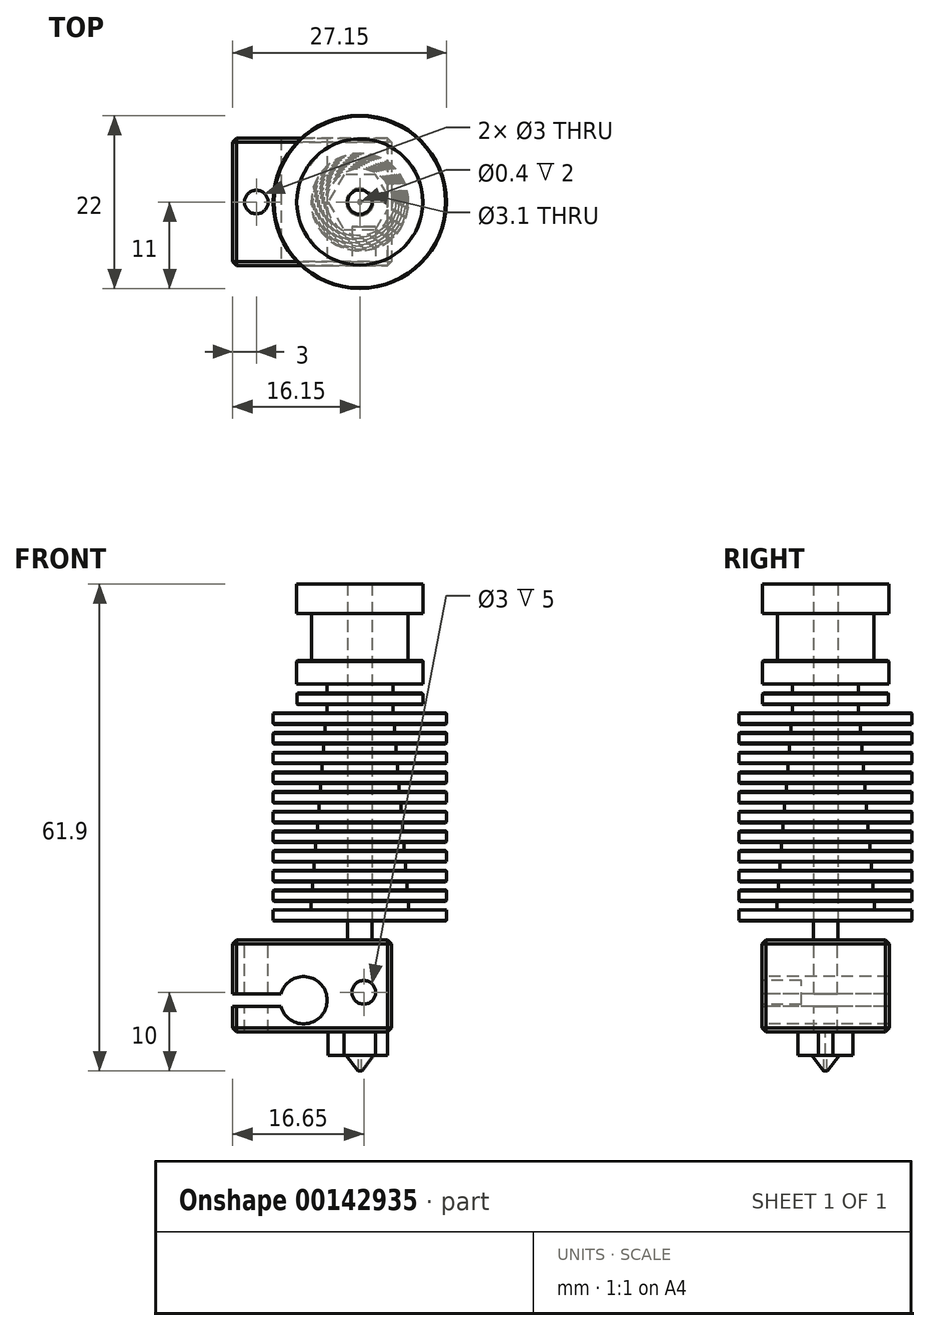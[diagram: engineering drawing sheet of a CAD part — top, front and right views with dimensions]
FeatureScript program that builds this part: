
annotation { "Feature Type Name" : "Feature", "Feature Type Description" : "" }
export const myFeature = defineFeature(function(context is Context, id is Id, definition is map)
    precondition{}
    {
        {
            var Q0;
            Q0=qCreatedBy(makeId("Top.planeOp"),FACE);
            var sketch = newSketch(context, id + "F0", { "sketchPlane" : qUnion([Q0])});
            skCircle(sketch, "E0", {"center": v(0, 0) * mm, "radius": 11 * mm});
            skCircle(sketch, "E1", {"center": v(0, 0) * mm, "radius": 1.55 * mm});
            skSolve(sketch);
        }
        {
            var Q0;
            Q0 = qSketchRegion(id + "F0", true);
            extrude(context, id + "F1", {"entities" : qUnion([Q0]), "depth" : 42.85 * mm});
        }
        {
            var Q0;
            Q0=qCreatedBy(makeId("Front.planeOp"),FACE);
            var sketch = newSketch(context, id + "F2", { "sketchPlane" : qUnion([Q0])});
            skLineSegment(sketch, "E2", {"start": v(11, 0) * mm, "end": v(11, 1.45) * mm});
            skLineSegment(sketch, "E3", {"start": v(11, 1.45) * mm, "end": v(6.2, 1.45) * mm});
            skLineSegment(sketch, "E4", {"start": v(6.2, 1.45) * mm, "end": v(6.2, 2.5) * mm});
            skLineSegment(sketch, "E5", {"start": v(6.2, 2.5) * mm, "end": v(11, 2.5) * mm});
            skLineSegment(sketch, "E6", {"start": v(11, 2.5) * mm, "end": v(11, 3.95) * mm});
            skLineSegment(sketch, "E7", {"start": v(11, 3.95) * mm, "end": v(6, 3.95) * mm});
            skLineSegment(sketch, "E8", {"start": v(6, 3.95) * mm, "end": v(6, 5) * mm});
            skLineSegment(sketch, "E9", {"start": v(6, 5) * mm, "end": v(11, 5) * mm});
            skLineSegment(sketch, "E10", {"start": v(11, 5) * mm, "end": v(11, 6.45) * mm});
            skLineSegment(sketch, "E11", {"start": v(11, 6.45) * mm, "end": v(5.8, 6.45) * mm});
            skLineSegment(sketch, "E12", {"start": v(5.8, 6.45) * mm, "end": v(5.8, 7.5) * mm});
            skLineSegment(sketch, "E13", {"start": v(5.8, 7.5) * mm, "end": v(11, 7.5) * mm});
            skLineSegment(sketch, "E14", {"start": v(11, 7.5) * mm, "end": v(11, 8.95) * mm});
            skLineSegment(sketch, "E15", {"start": v(11, 8.95) * mm, "end": v(5.6, 8.95) * mm});
            skLineSegment(sketch, "E16", {"start": v(5.6, 8.95) * mm, "end": v(5.6, 10) * mm});
            skLineSegment(sketch, "E17", {"start": v(5.6, 10) * mm, "end": v(11, 10) * mm});
            skLineSegment(sketch, "E18", {"start": v(11, 10) * mm, "end": v(11, 11.45) * mm});
            skLineSegment(sketch, "E19", {"start": v(11, 11.45) * mm, "end": v(5.4, 11.45) * mm});
            skLineSegment(sketch, "E20", {"start": v(5.4, 11.45) * mm, "end": v(5.4, 12.5) * mm});
            skLineSegment(sketch, "E21", {"start": v(5.4, 12.5) * mm, "end": v(11, 12.5) * mm});
            skLineSegment(sketch, "E22", {"start": v(11, 12.5) * mm, "end": v(11, 13.95) * mm});
            skLineSegment(sketch, "E23", {"start": v(11, 13.95) * mm, "end": v(5.2, 13.95) * mm});
            skLineSegment(sketch, "E24", {"start": v(5.2, 13.95) * mm, "end": v(5.2, 15) * mm});
            skLineSegment(sketch, "E25", {"start": v(5.2, 15) * mm, "end": v(11, 15) * mm});
            skLineSegment(sketch, "E26", {"start": v(11, 15) * mm, "end": v(11, 16.45) * mm});
            skLineSegment(sketch, "E27", {"start": v(11, 16.45) * mm, "end": v(5, 16.45) * mm});
            skLineSegment(sketch, "E28", {"start": v(5, 16.45) * mm, "end": v(5, 17.5) * mm});
            skLineSegment(sketch, "E29", {"start": v(5, 17.5) * mm, "end": v(11, 17.5) * mm});
            skLineSegment(sketch, "E30", {"start": v(11, 17.5) * mm, "end": v(11, 18.95) * mm});
            skLineSegment(sketch, "E31", {"start": v(11, 18.95) * mm, "end": v(4.8, 18.95) * mm});
            skLineSegment(sketch, "E32", {"start": v(4.8, 18.95) * mm, "end": v(4.8, 20) * mm});
            skLineSegment(sketch, "E33", {"start": v(4.8, 20) * mm, "end": v(11, 20) * mm});
            skLineSegment(sketch, "E34", {"start": v(11, 20) * mm, "end": v(11, 21.45) * mm});
            skLineSegment(sketch, "E35", {"start": v(11, 21.45) * mm, "end": v(4.6, 21.45) * mm});
            skLineSegment(sketch, "E36", {"start": v(4.6, 21.45) * mm, "end": v(4.6, 22.5) * mm});
            skLineSegment(sketch, "E37", {"start": v(4.6, 22.5) * mm, "end": v(11, 22.5) * mm});
            skLineSegment(sketch, "E38", {"start": v(11, 22.5) * mm, "end": v(11, 23.95) * mm});
            skLineSegment(sketch, "E39", {"start": v(11, 23.95) * mm, "end": v(4.4, 23.95) * mm});
            skLineSegment(sketch, "E40", {"start": v(4.4, 23.95) * mm, "end": v(4.4, 25) * mm});
            skLineSegment(sketch, "E41", {"start": v(4.4, 25) * mm, "end": v(11, 25) * mm});
            skLineSegment(sketch, "E42", {"start": v(11, 25) * mm, "end": v(11, 26.45) * mm});
            skLineSegment(sketch, "E43", {"start": v(11, 26.45) * mm, "end": v(4.2, 26.45) * mm});
            skLineSegment(sketch, "E44", {"start": v(4.2, 26.45) * mm, "end": v(4.2, 27.5) * mm});
            skLineSegment(sketch, "E45", {"start": v(4.2, 27.5) * mm, "end": v(8, 27.5) * mm});
            skLineSegment(sketch, "E46", {"start": v(8, 27.5) * mm, "end": v(8, 28.95) * mm});
            skLineSegment(sketch, "E47", {"start": v(8, 28.95) * mm, "end": v(4.2, 28.95) * mm});
            skLineSegment(sketch, "E48", {"start": v(4.2, 28.95) * mm, "end": v(4.2, 30.1) * mm});
            skLineSegment(sketch, "E49", {"start": v(4.2, 30.1) * mm, "end": v(8.02, 30.1) * mm});
            skLineSegment(sketch, "E50", {"start": v(8.02, 30.1) * mm, "end": v(8.02, 33.1) * mm});
            skLineSegment(sketch, "E51", {"start": v(8.02, 33.1) * mm, "end": v(6.13, 33.1) * mm});
            skLineSegment(sketch, "E52", {"start": v(6.13, 33.1) * mm, "end": v(6.13, 39.1) * mm});
            skLineSegment(sketch, "E53", {"start": v(6.13, 39.1) * mm, "end": v(8.02, 39.1) * mm});
            skLineSegment(sketch, "E54", {"start": v(8.02, 39.1) * mm, "end": v(8.02, 42.85) * mm});
            skLineSegment(sketch, "E55", {"start": v(8.02, 42.85) * mm, "end": v(14.4, 42.85) * mm});
            skLineSegment(sketch, "E56", {"start": v(14.4, 42.85) * mm, "end": v(14.4, 0) * mm});
            skLineSegment(sketch, "E57", {"start": v(14.4, 0) * mm, "end": v(11, 0) * mm});
            skSolve(sketch);
        }
        {
            var Q0;
            Q0 = qSketchRegion(id + "F2", true);
            var Q1;
            Q1=makeQuery(id+"F1.opExtrude","SWEPT_FACE",FACE,{"disambiguationData":[OSD([sQuery(id+"F0.wireOp",EDGE,"E0")])]});
            revolve(context, id + "F3", {"operationType" : NewBodyOperationType.REMOVE, "entities" : qUnion([Q0]), "axis" : qUnion([Q1]), "revolveType" : RevolveType.FULL, "oppositeDirection" : true});
        }
        {
            var Q0;
            Q0=makeQuery(id+"F3.boolean.opBoolean","COPY",EDGE,{"derivedFrom":makeQuery(id+"F3.opRevolve","SWEPT_EDGE",EDGE,{"disambiguationData":[OSD([sQuery(id+"F2.wireOp",EDGE,"E54"),sQuery(id+"F2.wireOp",EDGE,"E55")])]})});
            var Q1;
            Q1=makeQuery(id+"F3.boolean.opBoolean","COPY",EDGE,{"derivedFrom":makeQuery(id+"F3.opRevolve","SWEPT_EDGE",EDGE,{"disambiguationData":[OSD([sQuery(id+"F2.wireOp",EDGE,"E50"),sQuery(id+"F2.wireOp",EDGE,"E51")])]})});
            var Q2;
            Q2=makeQuery(id+"F3.boolean.opBoolean","COPY",EDGE,{"derivedFrom":makeQuery(id+"F3.opRevolve","SWEPT_EDGE",EDGE,{"disambiguationData":[OSD([sQuery(id+"F2.wireOp",EDGE,"E46"),sQuery(id+"F2.wireOp",EDGE,"E47")])]})});
            var Q3;
            Q3=makeQuery(id+"F3.boolean.opBoolean","COPY",EDGE,{"derivedFrom":makeQuery(id+"F3.opRevolve","SWEPT_EDGE",EDGE,{"disambiguationData":[OSD([sQuery(id+"F2.wireOp",EDGE,"E45"),sQuery(id+"F2.wireOp",EDGE,"E46")])]})});
            var Q4;
            Q4=makeQuery(id+"F3.boolean.opBoolean","COPY",EDGE,{"derivedFrom":makeQuery(id+"F3.opRevolve","SWEPT_EDGE",EDGE,{"disambiguationData":[OSD([sQuery(id+"F2.wireOp",EDGE,"E42"),sQuery(id+"F2.wireOp",EDGE,"E43")])]})});
            var Q5;
            Q5=makeQuery(id+"F3.boolean.opBoolean","COPY",EDGE,{"derivedFrom":makeQuery(id+"F3.opRevolve","SWEPT_EDGE",EDGE,{"disambiguationData":[OSD([sQuery(id+"F2.wireOp",EDGE,"E41"),sQuery(id+"F2.wireOp",EDGE,"E42")])]})});
            var Q6;
            Q6=makeQuery(id+"F3.boolean.opBoolean","COPY",EDGE,{"derivedFrom":makeQuery(id+"F3.opRevolve","SWEPT_EDGE",EDGE,{"disambiguationData":[OSD([sQuery(id+"F2.wireOp",EDGE,"E38"),sQuery(id+"F2.wireOp",EDGE,"E39")])]})});
            var Q7;
            Q7=makeQuery(id+"F3.boolean.opBoolean","COPY",EDGE,{"derivedFrom":makeQuery(id+"F3.opRevolve","SWEPT_EDGE",EDGE,{"disambiguationData":[OSD([sQuery(id+"F2.wireOp",EDGE,"E37"),sQuery(id+"F2.wireOp",EDGE,"E38")])]})});
            var Q8;
            Q8=makeQuery(id+"F3.boolean.opBoolean","COPY",EDGE,{"derivedFrom":makeQuery(id+"F3.opRevolve","SWEPT_EDGE",EDGE,{"disambiguationData":[OSD([sQuery(id+"F2.wireOp",EDGE,"E34"),sQuery(id+"F2.wireOp",EDGE,"E35")])]})});
            var Q9;
            Q9=makeQuery(id+"F3.boolean.opBoolean","COPY",EDGE,{"derivedFrom":makeQuery(id+"F3.opRevolve","SWEPT_EDGE",EDGE,{"disambiguationData":[OSD([sQuery(id+"F2.wireOp",EDGE,"E33"),sQuery(id+"F2.wireOp",EDGE,"E34")])]})});
            var Q10;
            Q10=makeQuery(id+"F3.boolean.opBoolean","COPY",EDGE,{"derivedFrom":makeQuery(id+"F3.opRevolve","SWEPT_EDGE",EDGE,{"disambiguationData":[OSD([sQuery(id+"F2.wireOp",EDGE,"E30"),sQuery(id+"F2.wireOp",EDGE,"E31")])]})});
            var Q11;
            Q11=makeQuery(id+"F3.boolean.opBoolean","COPY",EDGE,{"derivedFrom":makeQuery(id+"F3.opRevolve","SWEPT_EDGE",EDGE,{"disambiguationData":[OSD([sQuery(id+"F2.wireOp",EDGE,"E29"),sQuery(id+"F2.wireOp",EDGE,"E30")])]})});
            var Q12;
            Q12=makeQuery(id+"F3.boolean.opBoolean","COPY",EDGE,{"derivedFrom":makeQuery(id+"F3.opRevolve","SWEPT_EDGE",EDGE,{"disambiguationData":[OSD([sQuery(id+"F2.wireOp",EDGE,"E26"),sQuery(id+"F2.wireOp",EDGE,"E27")])]})});
            var Q13;
            Q13=makeQuery(id+"F3.boolean.opBoolean","COPY",EDGE,{"derivedFrom":makeQuery(id+"F3.opRevolve","SWEPT_EDGE",EDGE,{"disambiguationData":[OSD([sQuery(id+"F2.wireOp",EDGE,"E25"),sQuery(id+"F2.wireOp",EDGE,"E26")])]})});
            var Q14;
            Q14=makeQuery(id+"F3.boolean.opBoolean","COPY",EDGE,{"derivedFrom":makeQuery(id+"F3.opRevolve","SWEPT_EDGE",EDGE,{"disambiguationData":[OSD([sQuery(id+"F2.wireOp",EDGE,"E22"),sQuery(id+"F2.wireOp",EDGE,"E23")])]})});
            var Q15;
            Q15=makeQuery(id+"F3.boolean.opBoolean","COPY",EDGE,{"derivedFrom":makeQuery(id+"F3.opRevolve","SWEPT_EDGE",EDGE,{"disambiguationData":[OSD([sQuery(id+"F2.wireOp",EDGE,"E21"),sQuery(id+"F2.wireOp",EDGE,"E22")])]})});
            var Q16;
            Q16=makeQuery(id+"F3.boolean.opBoolean","COPY",EDGE,{"derivedFrom":makeQuery(id+"F3.opRevolve","SWEPT_EDGE",EDGE,{"disambiguationData":[OSD([sQuery(id+"F2.wireOp",EDGE,"E18"),sQuery(id+"F2.wireOp",EDGE,"E19")])]})});
            var Q17;
            Q17=makeQuery(id+"F3.boolean.opBoolean","COPY",EDGE,{"derivedFrom":makeQuery(id+"F3.opRevolve","SWEPT_EDGE",EDGE,{"disambiguationData":[OSD([sQuery(id+"F2.wireOp",EDGE,"E17"),sQuery(id+"F2.wireOp",EDGE,"E18")])]})});
            var Q18;
            Q18=makeQuery(id+"F3.boolean.opBoolean","COPY",EDGE,{"derivedFrom":makeQuery(id+"F3.opRevolve","SWEPT_EDGE",EDGE,{"disambiguationData":[OSD([sQuery(id+"F2.wireOp",EDGE,"E14"),sQuery(id+"F2.wireOp",EDGE,"E15")])]})});
            var Q19;
            Q19=makeQuery(id+"F3.boolean.opBoolean","COPY",EDGE,{"derivedFrom":makeQuery(id+"F3.opRevolve","SWEPT_EDGE",EDGE,{"disambiguationData":[OSD([sQuery(id+"F2.wireOp",EDGE,"E13"),sQuery(id+"F2.wireOp",EDGE,"E14")])]})});
            var Q20;
            Q20=makeQuery(id+"F3.boolean.opBoolean","COPY",EDGE,{"derivedFrom":makeQuery(id+"F3.opRevolve","SWEPT_EDGE",EDGE,{"disambiguationData":[OSD([sQuery(id+"F2.wireOp",EDGE,"E10"),sQuery(id+"F2.wireOp",EDGE,"E11")])]})});
            var Q21;
            Q21=makeQuery(id+"F3.boolean.opBoolean","COPY",EDGE,{"derivedFrom":makeQuery(id+"F3.opRevolve","SWEPT_EDGE",EDGE,{"disambiguationData":[OSD([sQuery(id+"F2.wireOp",EDGE,"E9"),sQuery(id+"F2.wireOp",EDGE,"E10")])]})});
            var Q22;
            Q22=makeQuery(id+"F3.boolean.opBoolean","COPY",EDGE,{"derivedFrom":makeQuery(id+"F3.opRevolve","SWEPT_EDGE",EDGE,{"disambiguationData":[OSD([sQuery(id+"F2.wireOp",EDGE,"E6"),sQuery(id+"F2.wireOp",EDGE,"E7")])]})});
            var Q23;
            Q23=makeQuery(id+"F3.boolean.opBoolean","COPY",EDGE,{"derivedFrom":makeQuery(id+"F3.opRevolve","SWEPT_EDGE",EDGE,{"disambiguationData":[OSD([sQuery(id+"F2.wireOp",EDGE,"E5"),sQuery(id+"F2.wireOp",EDGE,"E6")])]})});
            var Q24;
            Q24=makeQuery(id+"F3.boolean.opBoolean","COPY",EDGE,{"derivedFrom":makeQuery(id+"F3.opRevolve","SWEPT_EDGE",EDGE,{"disambiguationData":[OSD([sQuery(id+"F2.wireOp",EDGE,"E2"),sQuery(id+"F2.wireOp",EDGE,"E3")])]})});
            var Q25;
            Q25=makeQuery(id+"F1.opExtrude","CAP_EDGE",EDGE,{"disambiguationData":[OSD([sQuery(id+"F0.wireOp",EDGE,"E0")])],"isStart":true});
            chamfer(context, id + "F4", {"entities" : qUnion([Q0, Q1, Q2, Q3, Q4, Q5, Q6, Q7, Q8, Q9, Q10, Q11, Q12, Q13, Q14, Q15, Q16, Q17, Q18, Q19, Q20, Q21, Q22, Q23, Q24, Q25]), "width" : .1 * mm, "tangentPropagation" : true});
        }
        {
            var Q0;
            Q0=qCreatedBy(makeId("Top.planeOp"),FACE);
            cPlane(context, id + "F5", {"entities" : qUnion([Q0]), "cplaneType" : CPlaneType.OFFSET, "offset" : 2.4 * mm, "oppositeDirection" : true, "width" : 150 * mm, "height" : 150 * mm});
        }
        {
            var Q0;
            Q0=makeQuery(id+"F0.imprint","IMPRINT",FACE,{"disambiguationData":[TD([[makeQuery(id+"F0.imprint","IMPRINT",EDGE,{"derivedFrom":sQuery(id+"F0.wireOp",EDGE,"E1")}),1.0]])]});
            extrude(context, id + "F6", {"entities" : qUnion([Q0]), "operationType" : NewBodyOperationType.ADD, "oppositeDirection" : true, "depth" : 2.4 * mm});
        }
        {
            var Q0;
            Q0=qCreatedBy(id+"F5.planeOp",FACE);
            var sketch = newSketch(context, id + "F7", { "sketchPlane" : qUnion([Q0])});
            skLineSegment(sketch, "E58.bottom", {"start": v(4, -8.1) * mm, "end": v(-16.15, -8.1) * mm});
            skLineSegment(sketch, "E58.top", {"start": v(4, 8.1) * mm, "end": v(-16.15, 8.1) * mm});
            skLineSegment(sketch, "E58.left", {"start": v(4, -8.1) * mm, "end": v(4, 8.1) * mm});
            skLineSegment(sketch, "E58.right", {"start": v(-16.15, -8.1) * mm, "end": v(-16.15, 8.1) * mm});
            skLineSegment(sketch, "E59", {"start": v(-16.15, 0) * mm, "end": v(4, 0) * mm, "construction": true});
            skLineSegment(sketch, "E60", {"start": v(0, -8.1) * mm, "end": v(0, 8.1) * mm, "construction": true});
            skLineSegment(sketch, "E61", {"start": v(-13.15, -8.1) * mm, "end": v(-13.15, 8.1) * mm, "construction": true});
            skCircle(sketch, "E62", {"center": v(-13.15, 0) * mm, "radius": 1.5 * mm});
            skSolve(sketch);
        }
        {
            var Q0;
            Q0=makeQuery(id+"F7.imprint","IMPRINT",FACE,{"disambiguationData":[TD([[makeQuery(id+"F7.imprint","IMPRINT",EDGE,{"derivedFrom":sQuery(id+"F7.wireOp",EDGE,"E58.bottom")}),-1.0]])]});
            extrude(context, id + "F8", {"entities" : qUnion([Q0]), "operationType" : NewBodyOperationType.ADD, "oppositeDirection" : true, "depth" : 11.65 * mm});
        }
        {
            var Q0;
            Q0=makeQuery(id+"F8.opExtrude","SWEPT_FACE",FACE,{"disambiguationData":[OSD([sQuery(id+"F7.wireOp",EDGE,"E58.bottom")])]});
            var sketch = newSketch(context, id + "F9", { "sketchPlane" : qUnion([Q0])});
            skCircle(sketch, "E63", {"center": v(0.5, -9.05) * mm, "radius": 1.5 * mm});
            skArc(sketch, "E64", {"start": v(-10.04, -10.85) * mm, "mid": v(-4.15, -10.05) * mm, "end": v(-10.04, -9.25) * mm});
            skLineSegment(sketch, "E65", {"start": v(-10.04, -9.25) * mm, "end": v(-16.15, -9.25) * mm});
            skLineSegment(sketch, "E66", {"start": v(-10.04, -10.85) * mm, "end": v(-16.15, -10.85) * mm});
            skSolve(sketch);
        }
        {
            var Q0;
            Q0 = qSketchRegion(id + "F9", true);
            extrude(context, id + "F10", {"entities" : qUnion([Q0]), "operationType" : NewBodyOperationType.REMOVE, "oppositeDirection" : true, "depth" : 5 * mm});
        }
        {
            var Q0;
            Q0=makeQuery(id+"F9.imprint","IMPRINT",FACE,{"disambiguationData":[TD([[makeQuery(id+"F9.imprint","IMPRINT",EDGE,{"derivedFrom":sQuery(id+"F9.wireOp",EDGE,"E64")}),1.0]])]});
            var Q1;
            Q1=makeQuery(id+"F8.opExtrude","SWEPT_FACE",FACE,{"disambiguationData":[OSD([sQuery(id+"F7.wireOp",EDGE,"E58.top")])]});
            extrude(context, id + "F11", {"entities" : qUnion([Q0]), "operationType" : NewBodyOperationType.REMOVE, "endBound" : BoundingType.UP_TO_SURFACE, "oppositeDirection" : true, "endBoundEntityFace" : qUnion([Q1]), "depth" : 25 * mm});
        }
        {
            var Q0;
            Q0=makeQuery(id+"F8.opExtrude","SWEPT_EDGE",EDGE,{"disambiguationData":[OSD([sQuery(id+"F7.wireOp",EDGE,"E58.bottom"),sQuery(id+"F7.wireOp",EDGE,"E58.left")])]});
            var Q1;
            Q1=makeQuery(id+"F8.opExtrude","CAP_EDGE",EDGE,{"disambiguationData":[OSD([sQuery(id+"F7.wireOp",EDGE,"E58.bottom")])],"isStart":true});
            var Q2;
            Q2=makeQuery(id+"F8.opExtrude","CAP_EDGE",EDGE,{"disambiguationData":[OSD([sQuery(id+"F7.wireOp",EDGE,"E58.bottom")])],"isStart":false});
            var Q3;
            Q3=makeQuery(id+"F8.opExtrude","CAP_EDGE",EDGE,{"disambiguationData":[OSD([sQuery(id+"F7.wireOp",EDGE,"E58.left")])],"isStart":false});
            var Q4;
            Q4=makeQuery(id+"F8.opExtrude","CAP_EDGE",EDGE,{"disambiguationData":[OSD([sQuery(id+"F7.wireOp",EDGE,"E58.left")])],"isStart":true});
            var Q5;
            {var subQ0=sQuery(id+"F7.wireOp",EDGE,"E58.bottom");var subQ1=sQuery(id+"F7.wireOp",EDGE,"E58.right");Q5=makeQuery(id+"F11.boolean.opBoolean","SPLIT",EDGE,{"disambiguationData":[TD([makeQuery(id+"F11.opExtrude","SWEPT_FACE",FACE,{"disambiguationData":[OSD([sQuery(id+"F9.wireOp",EDGE,"E65")])]})])],"derivedFrom":makeQuery(id+"F8.opExtrude","SWEPT_EDGE",EDGE,{"disambiguationData":[OSD([subQ0,subQ1])]})});}
            var Q6;
            {var subQ0=sQuery(id+"F7.wireOp",EDGE,"E58.bottom");var subQ1=sQuery(id+"F7.wireOp",EDGE,"E58.right");Q6=makeQuery(id+"F11.boolean.opBoolean","SPLIT",EDGE,{"disambiguationData":[TD([makeQuery(id+"F11.opExtrude","SWEPT_FACE",FACE,{"disambiguationData":[OSD([sQuery(id+"F9.wireOp",EDGE,"E66")])]})])],"derivedFrom":makeQuery(id+"F8.opExtrude","SWEPT_EDGE",EDGE,{"disambiguationData":[OSD([subQ0,subQ1])]})});}
            var Q7;
            Q7=makeQuery(id+"F8.opExtrude","CAP_EDGE",EDGE,{"disambiguationData":[OSD([sQuery(id+"F7.wireOp",EDGE,"E58.right")])],"isStart":true});
            var Q8;
            {var subQ0=sQuery(id+"F7.wireOp",EDGE,"E58.right");var subQ1=sQuery(id+"F7.wireOp",EDGE,"E58.top");Q8=makeQuery(id+"F11.boolean.opBoolean","SPLIT",EDGE,{"disambiguationData":[TD([makeQuery(id+"F11.opExtrude","SWEPT_FACE",FACE,{"disambiguationData":[OSD([sQuery(id+"F9.wireOp",EDGE,"E65")])]})])],"derivedFrom":makeQuery(id+"F8.opExtrude","SWEPT_EDGE",EDGE,{"disambiguationData":[OSD([subQ1,subQ0])]})});}
            var Q9;
            {var subQ0=sQuery(id+"F7.wireOp",EDGE,"E58.right");var subQ1=sQuery(id+"F7.wireOp",EDGE,"E58.top");Q9=makeQuery(id+"F11.boolean.opBoolean","SPLIT",EDGE,{"disambiguationData":[TD([makeQuery(id+"F11.opExtrude","SWEPT_FACE",FACE,{"disambiguationData":[OSD([sQuery(id+"F9.wireOp",EDGE,"E66")])]})])],"derivedFrom":makeQuery(id+"F8.opExtrude","SWEPT_EDGE",EDGE,{"disambiguationData":[OSD([subQ1,subQ0])]})});}
            var Q10;
            Q10=makeQuery(id+"F8.opExtrude","CAP_EDGE",EDGE,{"disambiguationData":[OSD([sQuery(id+"F7.wireOp",EDGE,"E58.top")])],"isStart":true});
            var Q11;
            Q11=makeQuery(id+"F8.opExtrude","SWEPT_EDGE",EDGE,{"disambiguationData":[OSD([sQuery(id+"F7.wireOp",EDGE,"E58.top"),sQuery(id+"F7.wireOp",EDGE,"E58.left")])]});
            var Q12;
            Q12=makeQuery(id+"F8.opExtrude","CAP_EDGE",EDGE,{"disambiguationData":[OSD([sQuery(id+"F7.wireOp",EDGE,"E58.top")])],"isStart":false});
            var Q13;
            Q13=makeQuery(id+"F8.opExtrude","CAP_EDGE",EDGE,{"disambiguationData":[OSD([sQuery(id+"F7.wireOp",EDGE,"E58.right")])],"isStart":false});
            chamfer(context, id + "F12", {"entities" : qUnion([Q0, Q1, Q2, Q3, Q4, Q5, Q6, Q7, Q8, Q9, Q10, Q11, Q12, Q13]), "width" : .5 * mm, "tangentPropagation" : true});
        }
        {
            var Q0;
            Q0=makeQuery(id+"F8.opExtrude","CAP_FACE",FACE,{"disambiguationData":[OSD([sQuery(id+"F7.wireOp",EDGE,"E58.bottom"),sQuery(id+"F7.wireOp",EDGE,"E58.top"),sQuery(id+"F7.wireOp",EDGE,"E58.left"),sQuery(id+"F7.wireOp",EDGE,"E58.right"),sQuery(id+"F7.wireOp",EDGE,"E62")])],"isStart":false});
            var sketch = newSketch(context, id + "F13", { "sketchPlane" : qUnion([Q0])});
            skCircle(sketch, "E67.cCircle", {"center": v(0, 0) * mm, "radius": 3.5 * mm, "construction": true});
            skLineSegment(sketch, "E67.0", {"start": v(2.02, -3.5) * mm, "end": v(-2.02, -3.5) * mm});
            skLineSegment(sketch, "E67.1", {"start": v(-2.02, -3.5) * mm, "end": v(-4.04, 0) * mm});
            skLineSegment(sketch, "E67.2", {"start": v(-4.04, 0) * mm, "end": v(-2.02, 3.5) * mm});
            skLineSegment(sketch, "E67.3", {"start": v(-2.02, 3.5) * mm, "end": v(2.02, 3.5) * mm});
            skLineSegment(sketch, "E67.4", {"start": v(2.02, 3.5) * mm, "end": v(4.04, 0) * mm});
            skLineSegment(sketch, "E67.5", {"start": v(4.04, 0) * mm, "end": v(2.02, -3.5) * mm});
            skPoint(sketch, "E67.0.midPoint", {"position": v(0, -3.5) * mm});
            skSolve(sketch);
        }
        {
            var Q0;
            {var subQ7=sQuery(id+"F13.wireOp",EDGE,"E67.0");Q0=makeQuery(id+"F13.imprint","IMPRINT",FACE,{"disambiguationData":[TD([[makeQuery(id+"F13.imprint","IMPRINT",EDGE,{"derivedFrom":subQ7}),-1.0]])]});}
            extrude(context, id + "F14", {"entities" : qUnion([Q0]), "operationType" : NewBodyOperationType.ADD, "depth" : 3 * mm});
        }
        {
            var Q0;
            Q0=makeQuery(id+"F14.opExtrude","CAP_FACE",FACE,{"disambiguationData":[OSD([sQuery(id+"F7.wireOp",EDGE,"E58.bottom"),sQuery(id+"F7.wireOp",EDGE,"E58.top"),sQuery(id+"F7.wireOp",EDGE,"E58.left"),sQuery(id+"F7.wireOp",EDGE,"E58.right"),sQuery(id+"F7.wireOp",EDGE,"E62"),sQuery(id+"F13.wireOp",EDGE,"E67.0"),sQuery(id+"F13.wireOp",EDGE,"E67.1"),sQuery(id+"F13.wireOp",EDGE,"E67.2"),sQuery(id+"F13.wireOp",EDGE,"E67.3"),sQuery(id+"F13.wireOp",EDGE,"E67.4"),sQuery(id+"F13.wireOp",EDGE,"E67.5")])],"isStart":false});
            var sketch = newSketch(context, id + "F15", { "sketchPlane" : qUnion([Q0])});
            skCircle(sketch, "E68", {"center": v(0, 0) * mm, "radius": 1.75 * mm});
            skCircle(sketch, "E69", {"center": v(0, 0) * mm, "radius": 0.2 * mm});
            skSolve(sketch);
        }
        {
            var Q0;
            Q0=makeQuery(id+"F15.imprint","IMPRINT",FACE,{"disambiguationData":[TD([[makeQuery(id+"F15.imprint","IMPRINT",EDGE,{"derivedFrom":sQuery(id+"F15.wireOp",EDGE,"E68")}),1.0]])]});
            extrude(context, id + "F16", {"entities" : qUnion([Q0]), "operationType" : NewBodyOperationType.ADD, "depth" : 2 * mm});
        }
        {
            var Q0;
            Q0=qCreatedBy(makeId("Right.planeOp"),FACE);
            var sketch = newSketch(context, id + "F17", { "sketchPlane" : qUnion([Q0])});
            skLineSegment(sketch, "E70", {"start": v(1.76, -17.05) * mm, "end": v(0.26, -19.05) * mm});
            skLineSegment(sketch, "E71", {"start": v(0.26, -19.05) * mm, "end": v(1.76, -19.05) * mm});
            skLineSegment(sketch, "E72", {"start": v(1.76, -19.05) * mm, "end": v(1.76, -17.05) * mm});
            skSolve(sketch);
        }
        {
            var Q0;
            Q0 = qSketchRegion(id + "F17", true);
            var Q1;
            Q1=makeQuery(id+"F16.opExtrude","CAP_EDGE",EDGE,{"disambiguationData":[OSD([sQuery(id+"F15.wireOp",EDGE,"E69")])],"isStart":false});
            revolve(context, id + "F18", {"operationType" : NewBodyOperationType.REMOVE, "entities" : qUnion([Q0]), "axis" : qUnion([Q1]), "revolveType" : RevolveType.FULL, "oppositeDirection" : true});
        }
    });
